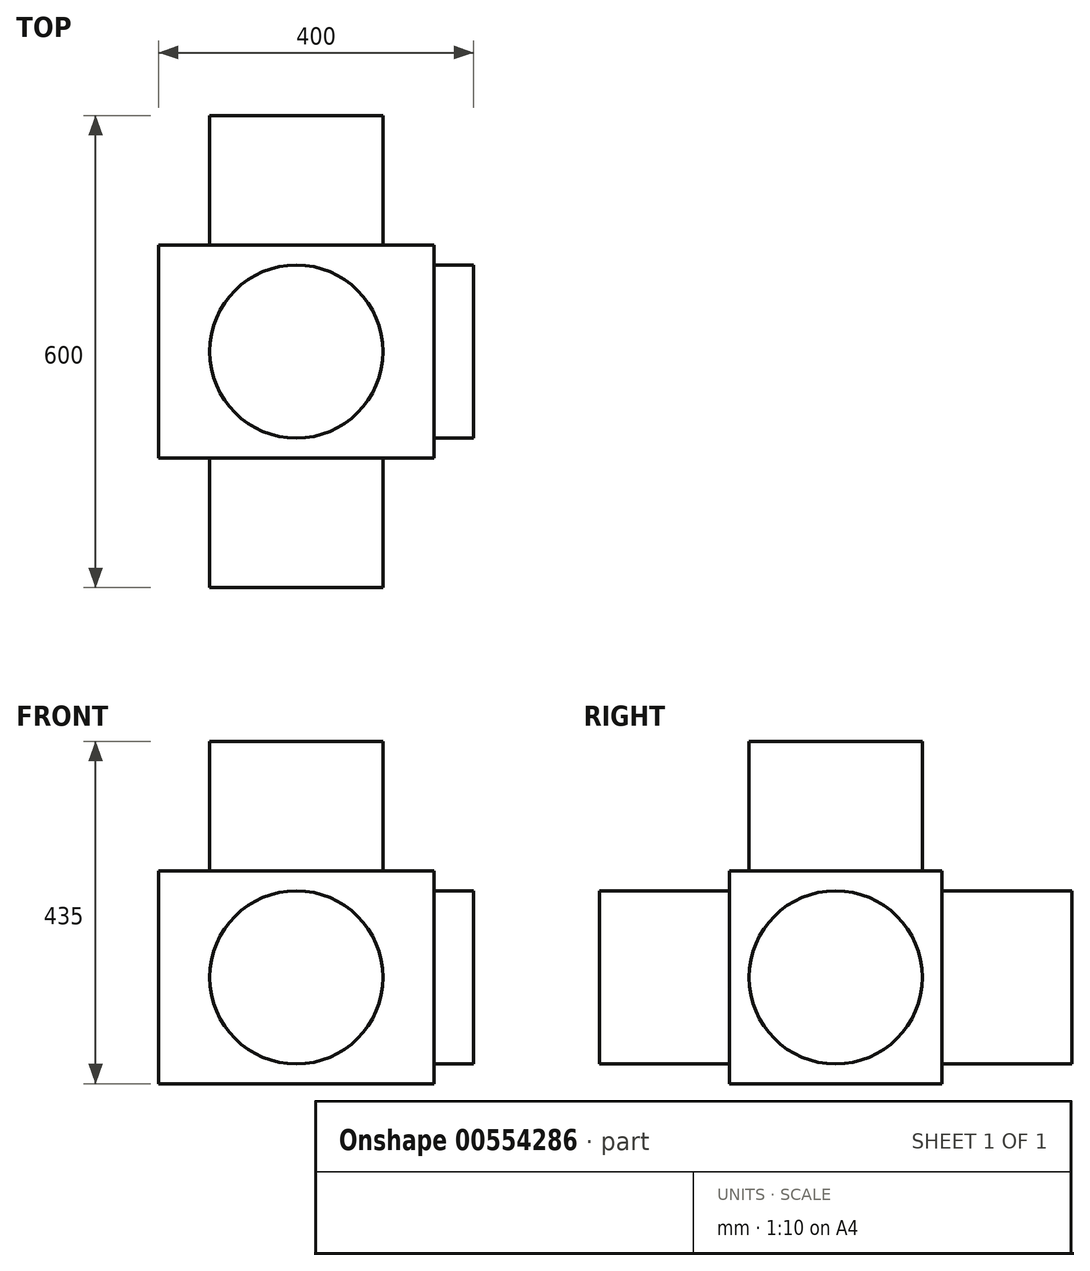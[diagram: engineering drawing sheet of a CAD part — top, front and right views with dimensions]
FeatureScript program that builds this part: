
annotation { "Feature Type Name" : "Feature", "Feature Type Description" : "" }
export const myFeature = defineFeature(function(context is Context, id is Id, definition is map)
    precondition{}
    {
        {
            var Q0;
            Q0=qCreatedBy(makeId("Front.planeOp"),FACE);
            var sketch = newSketch(context, id + "F0", { "sketchPlane" : qUnion([Q0])});
            skCircle(sketch, "E0", {"center": v(0, 0) * mm, "radius": 110 * mm});
            skSolve(sketch);
        }
        {
            var Q0;
            Q0=makeQuery(id+"F0.imprint","IMPRINT",FACE,{"disambiguationData":[TD([[makeQuery(id+"F0.imprint","IMPRINT",EDGE,{"derivedFrom":sQuery(id+"F0.wireOp",EDGE,"E0")}),1.0]])]});
            extrude(context, id + "F1", {"entities" : qUnion([Q0]), "endBound" : BoundingType.SYMMETRIC, "depth" : 600 * mm, "offsetDistance" : 25 * mm});
        }
        {
            var Q0;
            Q0=qCreatedBy(makeId("Top.planeOp"),FACE);
            var sketch = newSketch(context, id + "F2", { "sketchPlane" : qUnion([Q0])});
            skCircle(sketch, "E1", {"center": v(0, 0) * mm, "radius": 110 * mm});
            skSolve(sketch);
        }
        {
            var Q0;
            Q0=makeQuery(id+"F2.imprint","IMPRINT",FACE,{"disambiguationData":[TD([[makeQuery(id+"F2.imprint","IMPRINT",EDGE,{"derivedFrom":sQuery(id+"F2.wireOp",EDGE,"E1")}),1.0]])]});
            extrude(context, id + "F3", {"entities" : qUnion([Q0]), "operationType" : NewBodyOperationType.ADD, "depth" : 300 * mm, "offsetDistance" : 25 * mm});
        }
        {
            var Q0;
            Q0=qCreatedBy(makeId("Right.planeOp"),FACE);
            var sketch = newSketch(context, id + "F4", { "sketchPlane" : qUnion([Q0])});
            skLineSegment(sketch, "E2.bottom", {"start": v(-135, 135) * mm, "end": v(135, 135) * mm});
            skLineSegment(sketch, "E2.top", {"start": v(-135, -135) * mm, "end": v(135, -135) * mm});
            skLineSegment(sketch, "E2.left", {"start": v(-135, 135) * mm, "end": v(-135, -135) * mm});
            skLineSegment(sketch, "E2.right", {"start": v(135, 135) * mm, "end": v(135, -135) * mm});
            skSolve(sketch);
        }
        {
            var Q0;
            Q0=makeQuery(id+"F4.imprint","IMPRINT",FACE,{"disambiguationData":[TD([[makeQuery(id+"F4.imprint","IMPRINT",EDGE,{"derivedFrom":sQuery(id+"F4.wireOp",EDGE,"E2.bottom")}),-1.0]])]});
            extrude(context, id + "F5", {"entities" : qUnion([Q0]), "operationType" : NewBodyOperationType.ADD, "endBound" : BoundingType.SYMMETRIC, "depth" : 350 * mm, "offsetDistance" : 25 * mm});
        }
        {
            var Q0;
            Q0=makeQuery(id+"F5.opExtrude","CAP_FACE",FACE,{"disambiguationData":[OSD([sQuery(id+"F4.wireOp",EDGE,"E2.bottom"),sQuery(id+"F4.wireOp",EDGE,"E2.top"),sQuery(id+"F4.wireOp",EDGE,"E2.left"),sQuery(id+"F4.wireOp",EDGE,"E2.right")])],"isStart":false});
            var sketch = newSketch(context, id + "F6", { "sketchPlane" : qUnion([Q0])});
            skCircle(sketch, "E3", {"center": v(0, 0) * mm, "radius": 110 * mm});
            skSolve(sketch);
        }
        {
            var Q0;
            Q0=makeQuery(id+"F6.imprint","IMPRINT",FACE,{"disambiguationData":[TD([[makeQuery(id+"F6.imprint","IMPRINT",EDGE,{"derivedFrom":sQuery(id+"F6.wireOp",EDGE,"E3")}),1.0]])]});
            extrude(context, id + "F7", {"entities" : qUnion([Q0]), "operationType" : NewBodyOperationType.ADD, "depth" : 50 * mm, "offsetDistance" : 25 * mm});
        }
    });
